# Revit family: Hager-Volta-IP30-Flush_mounted-leer-NoHosted-DE-de
name_source: partatom
category: Electrical Equipment
units: mm (PartAtom-declared; Revit-internal decimal feet)

## family parameters
Always vertical = Yes
Cut with Voids When Loaded = No
Panel Configuration = Two Columns, Circuits Across
Part Type = Panelboard
Room Calculation Point = No
Round Connector Dimension = Use Diameter
Shared = No
Work Plane-Based = Yes

## types (22) — shared parameters
Default Elevation = 1219 mm
EF000003 - Montageart = EV000383 - Unterputz
EF001088 - Anbaumöglichkeit = Yes
EF001131 - Innentiefe = 92 mm  [stored 0.301837 ft]
EF002950 - Breite in Teilungseinheiten = 12
EF006244 - Transparenter Deckel/Tür = No
EF006306 - Mit Schloss = No
EF015776 - Erdungsklemmenblock = No
EF015777 - Neutralleiterklemmenblock = No
HG000003 - Bereich = Volta
HG000005 - Dicke = 3 mm  [stored 0.00984252 ft]
HG000006 - Unterputz = Yes
HG000009 - Doppelflügeligen Tür = No
HG000010 - Asymmetrische Türen = No
HG000011 - Leere Reihen von unten = No
HG000017 - Distanz zwischen den Polen = 18 mm  [stored 0.0590551 ft]
Manufacturer = Hager
Type Comments = Volta
zero-valued in all types: HG000001 - Anzahl der Spalten, HG000007 - Anzahl der leeren Spalten, HG000008 - Anzahl der leeren Reihen

## per-type parameters (varying)
| type | EF000007 - Farbe | EF000008 - Breite | EF000040 - Höhe | EF000049 - Tiefe | EF000116 - RAL-Nummer | EF000118 - Mit Montageplatte | EF000218 - Einbautiefe | EF000266 - Anzahl der Reihen | EF000332 - Einbauhöhe | EF000339 - Art der Abdeckung | EF000846 - Einbaubreite | EF001062 - EMV-Ausführung | EF001134 - DIN-Schiene | EF001596 - Werkstoff des Gehäuses | EF004462 - Art der Schließung | EF005474 - Schutzart (IP) | EF009212 - Ausführung Deckel | EF015941 - Signaldurchlassende Tür | HG000002 - Mit tür | HG000004 - Herstellerreferenz | Model |
| Unterputz  B330 H355 T94.5 12 Teilungseinheiten - VU12NK | EV000270 - grau | 330 mm | 355 mm | 94 mm  [stored 0.308399 ft] | 7035 | No | 90 mm  [stored 0.295276 ft] | 1 | 346 mm  [stored 1.13517 ft] |  | 335 mm  [stored 1.09908 ft] | Yes | No | EV000139 - Kunststoff |  |  | EV000116 - geschlossen | No | No | VU12NK | VU12NK |
| Unterputz  B330 H484 T94.5 12 Teilungseinheiten - VU24NK | EV000270 - grau | 330 mm | 484 mm  [stored 1.58793 ft] | 94 mm  [stored 0.308399 ft] | 7035 | No | 90 mm  [stored 0.295276 ft] | 2 | 471 mm  [stored 1.54528 ft] |  | 335 mm  [stored 1.09908 ft] | Yes | No | EV000139 - Kunststoff |  |  | EV000116 - geschlossen | No | No | VU24NK | VU24NK |
| Unterputz  B330 H609 T94.5 12 Teilungseinheiten - VU36NK | EV000270 - grau | 330 mm | 609 mm  [stored 1.99803 ft] | 94 mm  [stored 0.308399 ft] | 7035 | No | 90 mm  [stored 0.295276 ft] | 3 | 596 mm  [stored 1.95538 ft] |  | 335 mm  [stored 1.09908 ft] | Yes | No | EV000139 - Kunststoff |  |  | EV000116 - geschlossen | No | No | VU36NK | VU36NK |
| Unterputz  B330 H734 T94.5 12 Teilungseinheiten - VU48NK | EV000270 - grau | 330 mm | 734 mm  [stored 2.40814 ft] | 94 mm  [stored 0.308399 ft] | 7035 | No | 90 mm  [stored 0.295276 ft] | 4 | 721 mm  [stored 2.36549 ft] |  | 335 mm  [stored 1.09908 ft] | Yes | No | EV000139 - Kunststoff |  |  | EV000116 - geschlossen | No | No | VU48NK | VU48NK |
| Unterputz  B348 H880 T94.5 12 Teilungseinheiten - VU60NK | EV000270 - grau | 348 mm  [stored 1.14173 ft] | 880 mm  [stored 2.88714 ft] | 94 mm  [stored 0.308399 ft] | 7035 | No | 90 mm  [stored 0.295276 ft] | 5 | 846 mm  [stored 2.77559 ft] |  | 335 mm  [stored 1.09908 ft] | Yes | No | EV000139 - Kunststoff |  |  | EV000116 - geschlossen | No | No | VU60NK | VU60NK |
| Unterputz IP30 B348 H505.5 T98 12 Teilungseinheiten - VU24NWB | EV000202 - weiß | 348 mm  [stored 1.14173 ft] | 506 mm  [stored 1.6601 ft] | 98 mm  [stored 0.321522 ft] | 9010 | Yes | 89 mm  [stored 0.291995 ft] | 0 | 470 mm  [stored 1.54199 ft] | EV004216 - Tür | 314 mm  [stored 1.03018 ft] | No | Yes | EV000154 - sonstige | EV000154 - sonstige | EV006410 - IP30 | EV009916 - mit Ausschnitt | No | Yes | VU24NWB | VU24NWB |
| Unterputz IP30 B348 H630.5 T98 12 Teilungseinheiten - VU36NKM | EV000270 - grau | 348 mm  [stored 1.14173 ft] | 630 mm  [stored 2.06693 ft] | 98 mm  [stored 0.321522 ft] | 7035 | Yes | 89 mm  [stored 0.291995 ft] | 0 | 595 mm  [stored 1.9521 ft] |  | 314 mm  [stored 1.03018 ft] | No | Yes | EV000139 - Kunststoff |  | EV006410 - IP30 | EV000116 - geschlossen | No | No | VU36NKM | VU36NKM |
| Unterputz IP30 B348 H630.5 T98 12 Teilungseinheiten - VU36NW | EV000202 - weiß | 348 mm  [stored 1.14173 ft] | 630 mm  [stored 2.06693 ft] | 98 mm  [stored 0.321522 ft] | 9010 | Yes | 89 mm  [stored 0.291995 ft] | 0 | 595 mm  [stored 1.9521 ft] | EV004216 - Tür | 314 mm  [stored 1.03018 ft] | No | Yes | EV000154 - sonstige | EV000154 - sonstige | EV006410 - IP30 | EV009916 - mit Ausschnitt | No | Yes | VU36NW | VU36NW |
| Unterputz IP30 B348 H630.5 T98 12 Teilungseinheiten - VU36NWB | EV000202 - weiß | 348 mm  [stored 1.14173 ft] | 630 mm  [stored 2.06693 ft] | 98 mm  [stored 0.321522 ft] | 9010 | Yes | 89 mm  [stored 0.291995 ft] | 0 | 595 mm  [stored 1.9521 ft] | EV004216 - Tür | 314 mm  [stored 1.03018 ft] | No | Yes | EV000154 - sonstige | EV000154 - sonstige | EV006410 - IP30 | EV009916 - mit Ausschnitt | No | Yes | VU36NWB | VU36NWB |
| Unterputz IP30 B348 H630.5 T98 12 Teilungseinheiten - VU36WWH | EV000202 - weiß | 348 mm  [stored 1.14173 ft] | 630 mm  [stored 2.06693 ft] | 98 mm  [stored 0.321522 ft] | 9010 | Yes | 89 mm  [stored 0.291995 ft] | 0 | 595 mm  [stored 1.9521 ft] | EV004216 - Tür | 314 mm  [stored 1.03018 ft] | No | Yes | EV000154 - sonstige | EV000154 - sonstige | EV006410 - IP30 | EV009916 - mit Ausschnitt | Yes | Yes | VU36WWH | VU36WWH |
| Unterputz IP30 B348 H755.5 T98 12 Teilungseinheiten - VU48MMV | EV000202 - weiß | 348 mm  [stored 1.14173 ft] | 756 mm  [stored 2.48031 ft] | 98 mm  [stored 0.321522 ft] | 9010 | Yes | 89 mm  [stored 0.291995 ft] | 0 | 720 mm  [stored 2.3622 ft] | EV004216 - Tür | 314 mm  [stored 1.03018 ft] | No | Yes | EV000154 - sonstige | EV000154 - sonstige | EV006410 - IP30 | EV009916 - mit Ausschnitt | No | Yes | VU48MMV | VU48MMV |
| Unterputz IP30 B348 H755.5 T98 12 Teilungseinheiten - VU48NKM | EV000270 - grau | 348 mm  [stored 1.14173 ft] | 756 mm  [stored 2.48031 ft] | 98 mm  [stored 0.321522 ft] | 7035 | Yes | 89 mm  [stored 0.291995 ft] | 0 | 720 mm  [stored 2.3622 ft] |  | 314 mm  [stored 1.03018 ft] | No | Yes | EV000139 - Kunststoff |  | EV006410 - IP30 | EV000116 - geschlossen | No | No | VU48NKM | VU48NKM |
| Unterputz IP30 B348 H755.5 T98 12 Teilungseinheiten - VU48NW | EV000202 - weiß | 348 mm  [stored 1.14173 ft] | 756 mm  [stored 2.48031 ft] | 98 mm  [stored 0.321522 ft] | 9010 | Yes | 89 mm  [stored 0.291995 ft] | 0 | 720 mm  [stored 2.3622 ft] | EV004216 - Tür | 314 mm  [stored 1.03018 ft] | No | Yes | EV000154 - sonstige | EV000154 - sonstige | EV006410 - IP30 | EV009916 - mit Ausschnitt | No | Yes | VU48NW | VU48NW |
| Unterputz IP30 B348 H755.5 T98 12 Teilungseinheiten - VU48NWB | EV000202 - weiß | 348 mm  [stored 1.14173 ft] | 756 mm  [stored 2.48031 ft] | 98 mm  [stored 0.321522 ft] | 9010 | Yes | 89 mm  [stored 0.291995 ft] | 0 | 720 mm  [stored 2.3622 ft] | EV004216 - Tür | 314 mm  [stored 1.03018 ft] | No | Yes | EV000154 - sonstige | EV000154 - sonstige | EV006410 - IP30 | EV009916 - mit Ausschnitt | No | Yes | VU48NWB | VU48NWB |
| Unterputz IP30 B348 H755.5 T98 12 Teilungseinheiten - VU48WWH | EV000202 - weiß | 348 mm  [stored 1.14173 ft] | 756 mm  [stored 2.48031 ft] | 98 mm  [stored 0.321522 ft] | 9010 | Yes | 89 mm  [stored 0.291995 ft] | 0 | 720 mm  [stored 2.3622 ft] | EV004216 - Tür | 314 mm  [stored 1.03018 ft] | No | Yes | EV000154 - sonstige | EV000154 - sonstige | EV006410 - IP30 | EV009916 - mit Ausschnitt | Yes | Yes | VU48WWH | VU48WWH |
| Unterputz IP30 B348 H755.5 T98 12 Teilungseinheiten - VU48WWV | EV000202 - weiß | 348 mm  [stored 1.14173 ft] | 756 mm  [stored 2.48031 ft] | 98 mm  [stored 0.321522 ft] | 9010 | Yes | 89 mm  [stored 0.291995 ft] | 0 | 720 mm  [stored 2.3622 ft] | EV004216 - Tür | 314 mm  [stored 1.03018 ft] | No | Yes | EV000154 - sonstige | EV000154 - sonstige | EV006410 - IP30 | EV009916 - mit Ausschnitt | Yes | Yes | VU48WWV | VU48WWV |
| Unterputz IP30 B348 H880.5 T98 12 Teilungseinheiten - VU60MMV | EV000202 - weiß | 348 mm  [stored 1.14173 ft] | 880 mm  [stored 2.88714 ft] | 98 mm  [stored 0.321522 ft] | 9010 | Yes | 89 mm  [stored 0.291995 ft] | 0 | 845 mm  [stored 2.77231 ft] | EV004216 - Tür | 314 mm  [stored 1.03018 ft] | No | Yes | EV000154 - sonstige | EV000154 - sonstige | EV006410 - IP30 | EV009916 - mit Ausschnitt | No | Yes | VU60MMV | VU60MMV |
| Unterputz IP30 B348 H880.5 T98 12 Teilungseinheiten - VU60NKM | EV000270 - grau | 348 mm  [stored 1.14173 ft] | 880 mm  [stored 2.88714 ft] | 98 mm  [stored 0.321522 ft] | 7035 | Yes | 89 mm  [stored 0.291995 ft] | 0 | 845 mm  [stored 2.77231 ft] |  | 314 mm  [stored 1.03018 ft] | No | Yes | EV000139 - Kunststoff |  | EV006410 - IP30 | EV000116 - geschlossen | No | No | VU60NKM | VU60NKM |
| Unterputz IP30 B348 H880.5 T98 12 Teilungseinheiten - VU60NW | EV000202 - weiß | 348 mm  [stored 1.14173 ft] | 880 mm  [stored 2.88714 ft] | 98 mm  [stored 0.321522 ft] | 9010 | Yes | 89 mm  [stored 0.291995 ft] | 0 | 845 mm  [stored 2.77231 ft] | EV004216 - Tür | 314 mm  [stored 1.03018 ft] | No | Yes | EV000154 - sonstige | EV000154 - sonstige | EV006410 - IP30 | EV009916 - mit Ausschnitt | No | Yes | VU60NW | VU60NW |
| Unterputz IP30 B348 H880.5 T98 12 Teilungseinheiten - VU60NWB | EV000202 - weiß | 348 mm  [stored 1.14173 ft] | 880 mm  [stored 2.88714 ft] | 98 mm  [stored 0.321522 ft] | 9010 | Yes | 89 mm  [stored 0.291995 ft] | 0 | 845 mm  [stored 2.77231 ft] | EV004216 - Tür | 314 mm  [stored 1.03018 ft] | No | Yes | EV000154 - sonstige | EV000154 - sonstige | EV006410 - IP30 | EV009916 - mit Ausschnitt | No | Yes | VU60NWB | VU60NWB |
| Unterputz IP30 B348 H880.5 T98 12 Teilungseinheiten - VU60WWH | EV000202 - weiß | 348 mm  [stored 1.14173 ft] | 880 mm  [stored 2.88714 ft] | 98 mm  [stored 0.321522 ft] | 9010 | Yes | 89 mm  [stored 0.291995 ft] | 0 | 845 mm  [stored 2.77231 ft] | EV004216 - Tür | 314 mm  [stored 1.03018 ft] | No | Yes | EV000154 - sonstige | EV000154 - sonstige | EV006410 - IP30 | EV009916 - mit Ausschnitt | Yes | Yes | VU60WWH | VU60WWH |
| Unterputz IP30 B348 H880.5 T98 12 Teilungseinheiten - VU60WWV | EV000202 - weiß | 348 mm  [stored 1.14173 ft] | 880 mm  [stored 2.88714 ft] | 98 mm  [stored 0.321522 ft] | 9010 | Yes | 89 mm  [stored 0.291995 ft] | 0 | 845 mm  [stored 2.77231 ft] | EV004216 - Tür | 314 mm  [stored 1.03018 ft] | No | Yes | EV000154 - sonstige | EV000154 - sonstige | EV006410 - IP30 | EV009916 - mit Ausschnitt | Yes | Yes | VU60WWV | VU60WWV |

note: [stored X ft] marks values corroborated as IEEE doubles in the binary element streams (Revit-internal decimal feet)

## geometry (parser evidence)
native form markers: Sweep x13
no freeform markers — native parametric forms only
